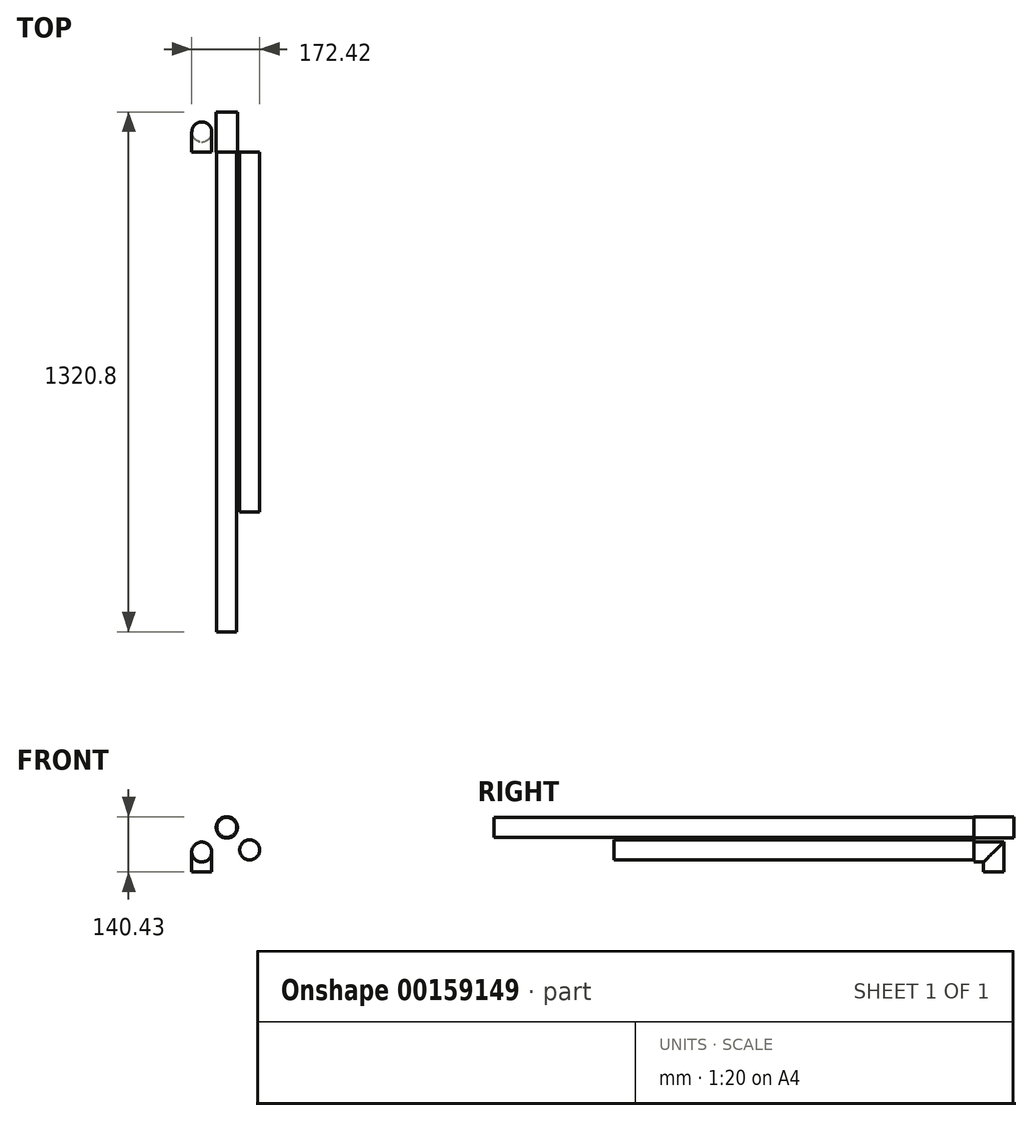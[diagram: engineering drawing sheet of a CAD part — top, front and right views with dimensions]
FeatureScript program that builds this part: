
annotation { "Feature Type Name" : "Feature", "Feature Type Description" : "" }
export const myFeature = defineFeature(function(context is Context, id is Id, definition is map)
    precondition{}
    {
        {
            var Q0;
            Q0=qCreatedBy(makeId("Front.planeOp"),FACE);
            var sketch = newSketch(context, id + "F0", { "sketchPlane" : qUnion([Q0])});
            skCircle(sketch, "E0", {"center": v(0, 0) * mm, "radius": 25.4 * mm});
            skSolve(sketch);
        }
        {
            var Q0;
            Q0=makeQuery(id+"F0.imprint","IMPRINT",FACE,{"disambiguationData":[TD([[makeQuery(id+"F0.imprint","IMPRINT",EDGE,{"derivedFrom":sQuery(id+"F0.wireOp",EDGE,"E0")}),1.0]])]});
            var Q1;
            Q1=sQuery(id+"F0.wireOp",EDGE,"E0");
            extrude(context, id + "F1", {"entities" : qUnion([Q0]), "surfaceEntities" : qUnion([Q1]), "depth" : 1219.2 * mm});
        }
        {
            var Q0;
            Q0=qCreatedBy(makeId("Front.planeOp"),FACE);
            var sketch = newSketch(context, id + "F2", { "sketchPlane" : qUnion([Q0])});
            skCircle(sketch, "E1", {"center": v(0, 0) * mm, "radius": 27.1 * mm});
            skSolve(sketch);
        }
        {
            var Q0;
            Q0=makeQuery(id+"F2.imprint","IMPRINT",FACE,{"disambiguationData":[TD([[makeQuery(id+"F2.imprint","IMPRINT",EDGE,{"derivedFrom":sQuery(id+"F2.wireOp",EDGE,"E1")}),1.0]])]});
            var Q1;
            Q1=sQuery(id+"F2.wireOp",EDGE,"E1");
            extrude(context, id + "F3", {"entities" : qUnion([Q0]), "surfaceEntities" : qUnion([Q1]), "oppositeDirection" : true, "depth" : 101.6 * mm});
        }
        {
            var Q0;
            Q0=qCreatedBy(makeId("Front.planeOp"),FACE);
            var sketch = newSketch(context, id + "F4", { "sketchPlane" : qUnion([Q0])});
            skCircle(sketch, "E2", {"center": v(-63.57, -62.53) * mm, "radius": 25.4 * mm});
            skSolve(sketch);
        }
        {
            var Q0;
            Q0=qCreatedBy(makeId("Right.planeOp"),FACE);
            var sketch = newSketch(context, id + "F5", { "sketchPlane" : qUnion([Q0])});
            skLineSegment(sketch, "E3", {"start": v(0, -62.53) * mm, "end": v(50.8, -62.53) * mm});
            skLineSegment(sketch, "E4", {"start": v(50.8, -62.53) * mm, "end": v(50.8, -113.33) * mm});
            skSolve(sketch);
        }
        {
            var Q0;
            Q0=makeQuery(id+"F4.imprint","IMPRINT",FACE,{"disambiguationData":[TD([[makeQuery(id+"F4.imprint","IMPRINT",EDGE,{"derivedFrom":sQuery(id+"F4.wireOp",EDGE,"E2")}),1.0]])]});
            var Q1;
            Q1=sQuery(id+"F4.wireOp",EDGE,"E2");
            var Q2;
            Q2=sQuery(id+"F5.wireOp",EDGE,"E3");
            var Q3;
            Q3=sQuery(id+"F5.wireOp",EDGE,"E4");
            sweep(context, id + "F6", {"profiles" : qUnion([Q0]), "surfaceProfiles" : qUnion([Q1]), "path" : qUnion([Q2, Q3])});
        }
        {
            var Q0;
            Q0=qCreatedBy(makeId("Front.planeOp"),FACE);
            var sketch = newSketch(context, id + "F7", { "sketchPlane" : qUnion([Q0])});
            skCircle(sketch, "E5", {"center": v(58.05, -57.2) * mm, "radius": 25.4 * mm});
            skSolve(sketch);
        }
        {
            var Q0;
            Q0=makeQuery(id+"F7.imprint","IMPRINT",FACE,{"disambiguationData":[TD([[makeQuery(id+"F7.imprint","IMPRINT",EDGE,{"derivedFrom":sQuery(id+"F7.wireOp",EDGE,"E5")}),1.0]])]});
            extrude(context, id + "F8", {"entities" : qUnion([Q0]), "depth" : 914.4 * mm});
        }
    });
